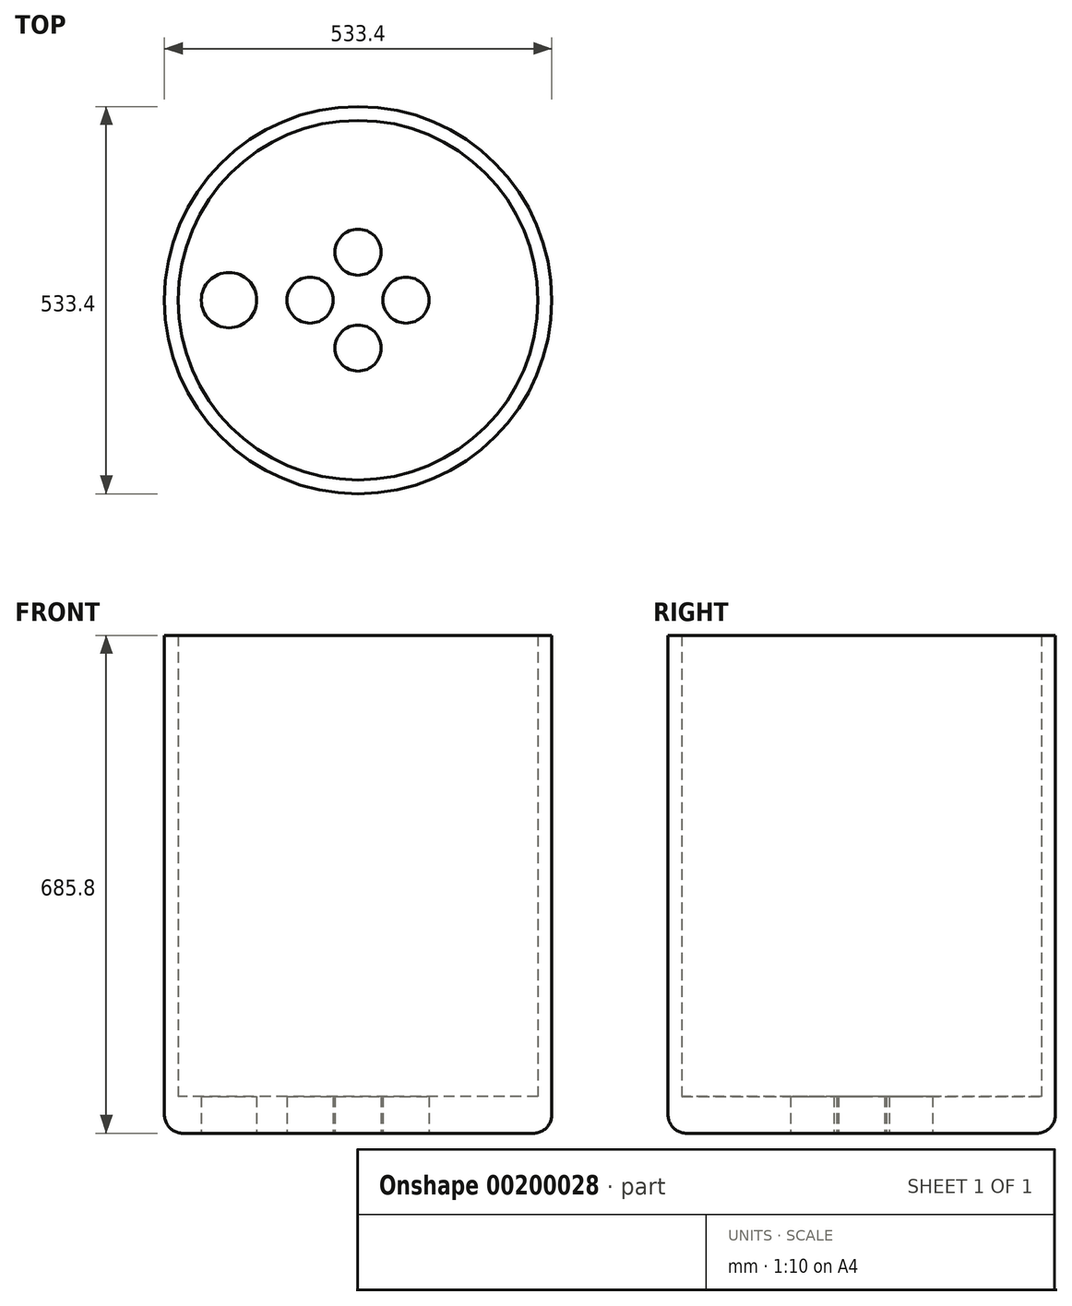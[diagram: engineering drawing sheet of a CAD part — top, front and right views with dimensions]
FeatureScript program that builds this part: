
annotation { "Feature Type Name" : "Feature", "Feature Type Description" : "" }
export const myFeature = defineFeature(function(context is Context, id is Id, definition is map)
    precondition{}
    {
        {
            var Q0;
            Q0=qCreatedBy(makeId("Top.planeOp"),FACE);
            var sketch = newSketch(context, id + "F0", { "sketchPlane" : qUnion([Q0])});
            skCircle(sketch, "E0", {"center": v(0, 0) * mm, "radius": 247.65 * mm});
            skCircle(sketch, "E1", {"center": v(0, 0) * mm, "radius": 266.7 * mm});
            skSolve(sketch);
        }
        {
            var Q0;
            Q0=makeQuery(id+"F0.imprint","IMPRINT",FACE,{"disambiguationData":[TD([[makeQuery(id+"F0.imprint","IMPRINT",EDGE,{"derivedFrom":sQuery(id+"F0.wireOp",EDGE,"E0")}),-1.0]])]});
            extrude(context, id + "F1", {"entities" : qUnion([Q0]), "depth" : 635 * mm});
        }
        {
            var Q0;
            Q0=makeQuery(id+"F1.opExtrude","CAP_FACE",FACE,{"disambiguationData":[OSD([sQuery(id+"F0.wireOp",EDGE,"E0"),sQuery(id+"F0.wireOp",EDGE,"E1")])],"isStart":true});
            var sketch = newSketch(context, id + "F2", { "sketchPlane" : qUnion([Q0])});
            skCircle(sketch, "E2", {"center": v(0, 0) * mm, "radius": 266.7 * mm});
            skSolve(sketch);
        }
        {
            var Q0;
            Q0 = qSketchRegion(id + "F2", true);
            extrude(context, id + "F3", {"entities" : qUnion([Q0]), "operationType" : NewBodyOperationType.ADD, "depth" : 50.8 * mm});
        }
        {
            var Q0;
            Q0=makeQuery(id+"F3.opExtrude","CAP_EDGE",EDGE,{"disambiguationData":[OSD([sQuery(id+"F2.wireOp",EDGE,"E2")])],"isStart":false});
            fillet(context, id + "F4", {"entities" : qUnion([Q0]), "radius" : 25.4 * mm, "tangentPropagation" : true, "allowEdgeOverflow" : false});
        }
        {
            var Q0;
            Q0=makeQuery(id+"F3.opExtrude","CAP_FACE",FACE,{"disambiguationData":[OSD([sQuery(id+"F2.wireOp",EDGE,"E2")])],"isStart":false});
            var sketch = newSketch(context, id + "F5", { "sketchPlane" : qUnion([Q0])});
            skCircle(sketch, "E3", {"center": v(-177.8, 0) * mm, "radius": 38.1 * mm});
            skSolve(sketch);
        }
        {
            var Q0;
            Q0=qCreatedBy(makeId("Front.planeOp"),FACE);
            var sketch = newSketch(context, id + "F6", { "sketchPlane" : qUnion([Q0])});
            skLineSegment(sketch, "E4", {"start": v(0, -64.6) * mm, "end": v(0, 279.96) * mm, "construction": true});
            skSolve(sketch);
        }
        {
            var Q0;
            Q0=makeQuery(id+"FHQC4g9FrUHuUaG_1.6.F5.imprint","IMPRINT",FACE,{"disambiguationData":[TD([[makeQuery(id+"FHQC4g9FrUHuUaG_1.6.F5.imprint","IMPRINT",EDGE,{"derivedFrom":sQuery(id+"FHQC4g9FrUHuUaG_1.6.F5.wireOp",EDGE,"E3")}),1.0]])]});
            var Q1;
            Q1=makeQuery(id+"FHQC4g9FrUHuUaG_1.4.F5.imprint","IMPRINT",FACE,{"disambiguationData":[TD([[makeQuery(id+"FHQC4g9FrUHuUaG_1.4.F5.imprint","IMPRINT",EDGE,{"derivedFrom":sQuery(id+"FHQC4g9FrUHuUaG_1.4.F5.wireOp",EDGE,"E3")}),1.0]])]});
            var Q2;
            Q2=makeQuery(id+"FHQC4g9FrUHuUaG_1.3.F5.imprint","IMPRINT",FACE,{"disambiguationData":[TD([[makeQuery(id+"FHQC4g9FrUHuUaG_1.3.F5.imprint","IMPRINT",EDGE,{"derivedFrom":sQuery(id+"FHQC4g9FrUHuUaG_1.3.F5.wireOp",EDGE,"E3")}),1.0]])]});
            var Q3;
            Q3=makeQuery(id+"FHQC4g9FrUHuUaG_1.2.F5.imprint","IMPRINT",FACE,{"disambiguationData":[TD([[makeQuery(id+"FHQC4g9FrUHuUaG_1.2.F5.imprint","IMPRINT",EDGE,{"derivedFrom":sQuery(id+"FHQC4g9FrUHuUaG_1.2.F5.wireOp",EDGE,"E3")}),1.0]])]});
            var Q4;
            Q4=makeQuery(id+"FHQC4g9FrUHuUaG_1.1.F5.imprint","IMPRINT",FACE,{"disambiguationData":[TD([[makeQuery(id+"FHQC4g9FrUHuUaG_1.1.F5.imprint","IMPRINT",EDGE,{"derivedFrom":sQuery(id+"FHQC4g9FrUHuUaG_1.1.F5.wireOp",EDGE,"E3")}),1.0]])]});
            var Q5;
            Q5=makeQuery(id+"F5.imprint","IMPRINT",FACE,{"disambiguationData":[TD([[makeQuery(id+"F5.imprint","IMPRINT",EDGE,{"derivedFrom":sQuery(id+"F5.wireOp",EDGE,"E3")}),1.0]])]});
            var Q6;
            Q6=makeQuery(id+"FHQC4g9FrUHuUaG_1.5.F5.imprint","IMPRINT",FACE,{"disambiguationData":[TD([[makeQuery(id+"FHQC4g9FrUHuUaG_1.5.F5.imprint","IMPRINT",EDGE,{"derivedFrom":sQuery(id+"FHQC4g9FrUHuUaG_1.5.F5.wireOp",EDGE,"E3")}),1.0]])]});
            var Q7;
            Q7=makeQuery(id+"FHQC4g9FrUHuUaG_1.7.F5.imprint","IMPRINT",FACE,{"disambiguationData":[TD([[makeQuery(id+"FHQC4g9FrUHuUaG_1.7.F5.imprint","IMPRINT",EDGE,{"derivedFrom":sQuery(id+"FHQC4g9FrUHuUaG_1.7.F5.wireOp",EDGE,"E3")}),1.0]])]});
            extrude(context, id + "F7", {"entities" : qUnion([Q0, Q1, Q2, Q3, Q4, Q5, Q6, Q7]), "operationType" : NewBodyOperationType.REMOVE, "endBound" : BoundingType.UP_TO_NEXT, "oppositeDirection" : true, "depth" : 25.4 * mm});
        }
        {
            var Q0;
            Q0=makeQuery(id+"F3.opExtrude","CAP_FACE",FACE,{"disambiguationData":[OSD([sQuery(id+"F2.wireOp",EDGE,"E2")])],"isStart":false});
            var sketch = newSketch(context, id + "F8", { "sketchPlane" : qUnion([Q0])});
            skCircle(sketch, "E5", {"center": v(66.04, 0) * mm, "radius": 31.75 * mm});
            skCircle(sketch, "E6.1.0", {"center": v(0, 66.04) * mm, "radius": 31.75 * mm});
            skCircle(sketch, "E6.2.0", {"center": v(-66.04, 0) * mm, "radius": 31.75 * mm});
            skCircle(sketch, "E6.3.0", {"center": v(0, -66.04) * mm, "radius": 31.75 * mm});
            skPoint(sketch, "E6.center", {"position": v(0, 0) * mm});
            skSolve(sketch);
        }
        {
            var Q0;
            Q0=makeQuery(id+"F8.imprint","IMPRINT",FACE,{"disambiguationData":[TD([[makeQuery(id+"F8.imprint","IMPRINT",EDGE,{"derivedFrom":sQuery(id+"F8.wireOp",EDGE,"E6.1.0")}),1.0]])]});
            var Q1;
            Q1=makeQuery(id+"F8.imprint","IMPRINT",FACE,{"disambiguationData":[TD([[makeQuery(id+"F8.imprint","IMPRINT",EDGE,{"derivedFrom":sQuery(id+"F8.wireOp",EDGE,"E5")}),1.0]])]});
            var Q2;
            Q2=makeQuery(id+"F8.imprint","IMPRINT",FACE,{"disambiguationData":[TD([[makeQuery(id+"F8.imprint","IMPRINT",EDGE,{"derivedFrom":sQuery(id+"F8.wireOp",EDGE,"E6.2.0")}),1.0]])]});
            var Q3;
            Q3=makeQuery(id+"F8.imprint","IMPRINT",FACE,{"disambiguationData":[TD([[makeQuery(id+"F8.imprint","IMPRINT",EDGE,{"derivedFrom":sQuery(id+"F8.wireOp",EDGE,"E6.3.0")}),1.0]])]});
            var Q4;
            Q4=sQuery(id+"F8.wireOp",EDGE,"E6.2.0");
            var Q5;
            Q5=sQuery(id+"F8.wireOp",EDGE,"E6.1.0");
            var Q6;
            Q6=sQuery(id+"F8.wireOp",EDGE,"E5");
            var Q7;
            Q7=sQuery(id+"F8.wireOp",EDGE,"E6.3.0");
            extrude(context, id + "F9", {"entities" : qUnion([Q0, Q1, Q2, Q3]), "operationType" : NewBodyOperationType.REMOVE, "surfaceEntities" : qUnion([Q4, Q5, Q6, Q7]), "endBound" : BoundingType.UP_TO_NEXT, "oppositeDirection" : true, "depth" : 25.4 * mm});
        }
    });
